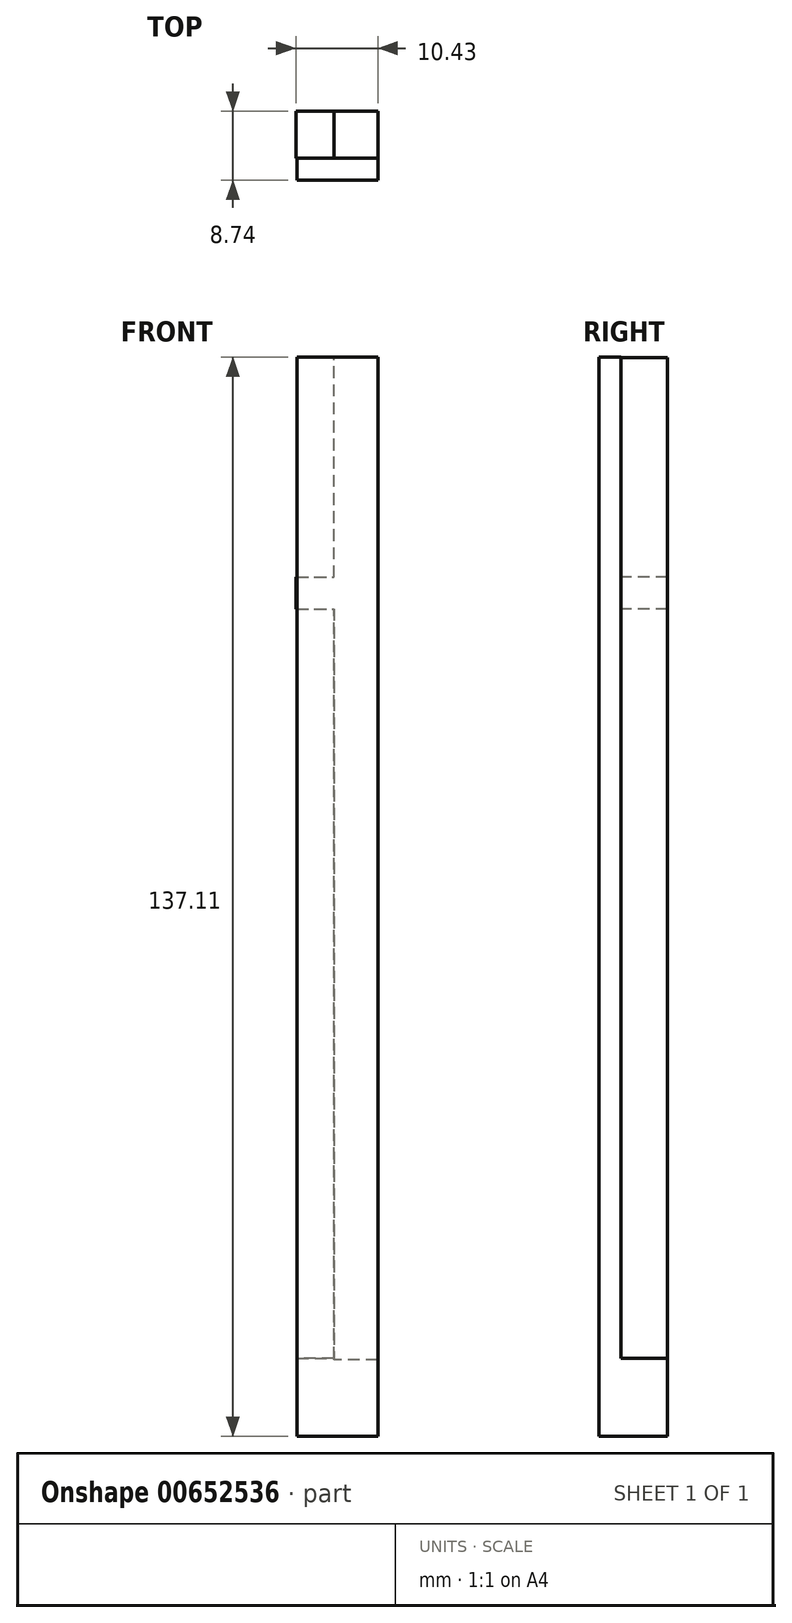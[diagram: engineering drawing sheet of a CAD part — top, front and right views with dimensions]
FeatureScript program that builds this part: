
annotation { "Feature Type Name" : "Feature", "Feature Type Description" : "" }
export const myFeature = defineFeature(function(context is Context, id is Id, definition is map)
    precondition{}
    {
        {
            var Q0;
            Q0=qCreatedBy(makeId("Front.planeOp"),FACE);
            var sketch = newSketch(context, id + "F0", { "sketchPlane" : qUnion([Q0])});
            skLineSegment(sketch, "E0.bottom", {"start": v(-4.7, 92.98) * mm, "end": v(5.6, 92.98) * mm});
            skLineSegment(sketch, "E0.top", {"start": v(-4.7, -34.22) * mm, "end": v(5.6, -34.22) * mm});
            skLineSegment(sketch, "E0.left", {"start": v(-4.7, 92.98) * mm, "end": v(-4.7, -34.22) * mm});
            skLineSegment(sketch, "E0.right", {"start": v(5.6, 92.98) * mm, "end": v(5.6, -34.22) * mm});
            skSolve(sketch);
        }
        {
            var Q0;
            Q0=makeQuery(id+"F0.imprint","IMPRINT",FACE,{"disambiguationData":[TD([[makeQuery(id+"F0.imprint","IMPRINT",EDGE,{"derivedFrom":sQuery(id+"F0.wireOp",EDGE,"E0.bottom")}),-1.0]])]});
            extrude(context, id + "F1", {"entities" : qUnion([Q0]), "oppositeDirection" : true, "depth" : 2.8 * mm, "offsetDistance" : 25.4 * mm});
        }
        {
            var Q0;
            Q0=qCreatedBy(makeId("Right.planeOp"),FACE);
            var sketch = newSketch(context, id + "F2", { "sketchPlane" : qUnion([Q0])});
            skLineSegment(sketch, "E1.bottom", {"start": v(0, 92.93) * mm, "end": v(8.74, 92.93) * mm});
            skLineSegment(sketch, "E1.top", {"start": v(0, -34.42) * mm, "end": v(8.74, -34.42) * mm});
            skLineSegment(sketch, "E1.left", {"start": v(0, 92.93) * mm, "end": v(0, -34.42) * mm});
            skLineSegment(sketch, "E1.right", {"start": v(8.74, 92.93) * mm, "end": v(8.74, -34.42) * mm});
            skSolve(sketch);
        }
        {
            var Q0;
            Q0 = qSketchRegion(id + "F2", true);
            extrude(context, id + "F3", {"entities" : qUnion([Q0]), "operationType" : NewBodyOperationType.ADD, "depth" : 5.6 * mm, "offsetDistance" : 25.4 * mm});
        }
        {
            var Q0;
            Q0=makeQuery(id+"F1.opExtrude","SWEPT_FACE",FACE,{"disambiguationData":[OSD([sQuery(id+"F0.wireOp",EDGE,"E0.top")])]});
            var sketch = newSketch(context, id + "F4", { "sketchPlane" : qUnion([Q0])});
            skLineSegment(sketch, "E2.bottom", {"start": v(5.6, 0) * mm, "end": v(-4.7, 0) * mm});
            skLineSegment(sketch, "E2.top", {"start": v(5.6, -8.73) * mm, "end": v(-4.7, -8.73) * mm});
            skLineSegment(sketch, "E2.left", {"start": v(5.6, 0) * mm, "end": v(5.6, -8.73) * mm});
            skLineSegment(sketch, "E2.right", {"start": v(-4.7, 0) * mm, "end": v(-4.7, -8.73) * mm});
            skSolve(sketch);
        }
        {
            var Q0;
            Q0 = qSketchRegion(id + "F4", true);
            extrude(context, id + "F5", {"entities" : qUnion([Q0]), "operationType" : NewBodyOperationType.ADD, "depth" : 9.9 * mm, "offsetDistance" : 25.4 * mm});
        }
        {
            var Q0;
            Q0=makeQuery(id+"F3.opExtrude","CAP_FACE",FACE,{"disambiguationData":[OSD([sQuery(id+"F2.wireOp",EDGE,"E1.bottom"),sQuery(id+"F2.wireOp",EDGE,"E1.top"),sQuery(id+"F2.wireOp",EDGE,"E1.left"),sQuery(id+"F2.wireOp",EDGE,"E1.right")])],"isStart":true});
            var sketch = newSketch(context, id + "F6", { "sketchPlane" : qUnion([Q0])});
            skLineSegment(sketch, "E3.bottom", {"start": v(-8.74, 65.01) * mm, "end": v(-2.8, 65.01) * mm});
            skLineSegment(sketch, "E3.top", {"start": v(-8.74, 61) * mm, "end": v(-2.8, 61) * mm});
            skLineSegment(sketch, "E3.left", {"start": v(-8.74, 65.01) * mm, "end": v(-8.74, 61) * mm});
            skLineSegment(sketch, "E3.right", {"start": v(-2.8, 65.01) * mm, "end": v(-2.8, 61) * mm});
            skSolve(sketch);
        }
        {
            var Q0;
            Q0 = qSketchRegion(id + "F6", true);
            extrude(context, id + "F7", {"entities" : qUnion([Q0]), "operationType" : NewBodyOperationType.ADD, "depth" : 4.83 * mm, "offsetDistance" : 25.4 * mm});
        }
    });
